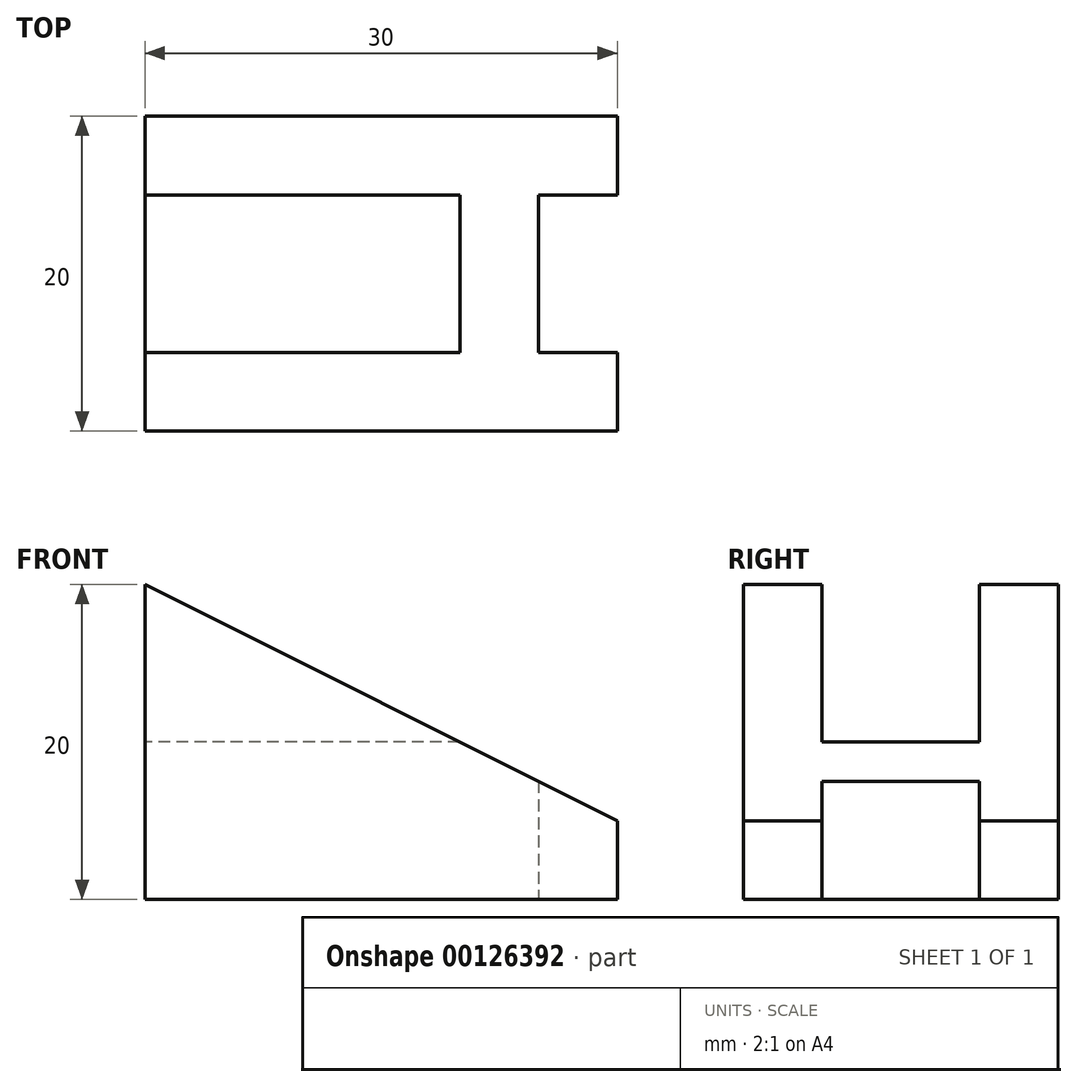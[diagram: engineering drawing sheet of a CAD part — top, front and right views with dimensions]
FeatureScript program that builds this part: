
annotation { "Feature Type Name" : "Feature", "Feature Type Description" : "" }
export const myFeature = defineFeature(function(context is Context, id is Id, definition is map)
    precondition{}
    {
        {
            var Q0;
            Q0=qCreatedBy(makeId("Top.planeOp"),FACE);
            var sketch = newSketch(context, id + "F0", { "sketchPlane" : qUnion([Q0])});
            skLineSegment(sketch, "E0.bottom", {"start": v(0, 0) * mm, "end": v(30, 0) * mm});
            skLineSegment(sketch, "E0.top", {"start": v(0, -20) * mm, "end": v(30, -20) * mm});
            skLineSegment(sketch, "E0.left", {"start": v(0, 0) * mm, "end": v(0, -20) * mm});
            skLineSegment(sketch, "E0.right", {"start": v(30, 0) * mm, "end": v(30, -20) * mm});
            skSolve(sketch);
        }
        {
            var Q0;
            Q0 = qSketchRegion(id + "F0", true);
            extrude(context, id + "F1", {"entities" : qUnion([Q0]), "depth" : 20 * mm});
        }
        {
            var Q0;
            Q0=makeQuery(id+"F1.opExtrude","SWEPT_FACE",FACE,{"disambiguationData":[OSD([sQuery(id+"F0.wireOp",EDGE,"E0.top")])]});
            var sketch = newSketch(context, id + "F2", { "sketchPlane" : qUnion([Q0])});
            skLineSegment(sketch, "E1", {"start": v(30, 20) * mm, "end": v(0, 20) * mm});
            skLineSegment(sketch, "E2", {"start": v(0, 20) * mm, "end": v(30, 5) * mm});
            skLineSegment(sketch, "E3", {"start": v(30, 5) * mm, "end": v(30, 20) * mm});
            skSolve(sketch);
        }
        {
            var Q0;
            Q0 = qSketchRegion(id + "F2", true);
            extrude(context, id + "F3", {"entities" : qUnion([Q0]), "operationType" : NewBodyOperationType.REMOVE, "oppositeDirection" : true, "depth" : 20 * mm});
        }
        {
            var Q0;
            Q0=makeQuery(id+"F1.opExtrude","SWEPT_FACE",FACE,{"disambiguationData":[OSD([sQuery(id+"F0.wireOp",EDGE,"E0.left")])]});
            var sketch = newSketch(context, id + "F4", { "sketchPlane" : qUnion([Q0])});
            skLineSegment(sketch, "E4", {"start": v(5, 20) * mm, "end": v(5, 10) * mm});
            skLineSegment(sketch, "E5", {"start": v(5, 10) * mm, "end": v(15, 10) * mm});
            skLineSegment(sketch, "E6", {"start": v(15, 10) * mm, "end": v(15, 20) * mm});
            skLineSegment(sketch, "E7", {"start": v(15, 20) * mm, "end": v(5, 20) * mm});
            skSolve(sketch);
        }
        {
            var Q0;
            Q0 = qSketchRegion(id + "F4", true);
            extrude(context, id + "F5", {"entities" : qUnion([Q0]), "operationType" : NewBodyOperationType.REMOVE, "endBound" : BoundingType.THROUGH_ALL, "oppositeDirection" : true, "depth" : 25 * mm});
        }
        {
            var Q0;
            Q0=makeQuery(id+"F1.opExtrude","CAP_FACE",FACE,{"disambiguationData":[OSD([sQuery(id+"F0.wireOp",EDGE,"E0.bottom"),sQuery(id+"F0.wireOp",EDGE,"E0.top"),sQuery(id+"F0.wireOp",EDGE,"E0.left"),sQuery(id+"F0.wireOp",EDGE,"E0.right")])],"isStart":true});
            var sketch = newSketch(context, id + "F6", { "sketchPlane" : qUnion([Q0])});
            skLineSegment(sketch, "E8", {"start": v(30, 15) * mm, "end": v(25, 15) * mm});
            skLineSegment(sketch, "E9", {"start": v(25, 15) * mm, "end": v(25, 5) * mm});
            skLineSegment(sketch, "E10", {"start": v(25, 5) * mm, "end": v(30, 5) * mm});
            skLineSegment(sketch, "E11", {"start": v(30, 5) * mm, "end": v(30, 15) * mm});
            skSolve(sketch);
        }
        {
            var Q0;
            Q0 = qSketchRegion(id + "F6", true);
            extrude(context, id + "F7", {"entities" : qUnion([Q0]), "operationType" : NewBodyOperationType.REMOVE, "endBound" : BoundingType.THROUGH_ALL, "oppositeDirection" : true, "depth" : 25 * mm});
        }
    });
